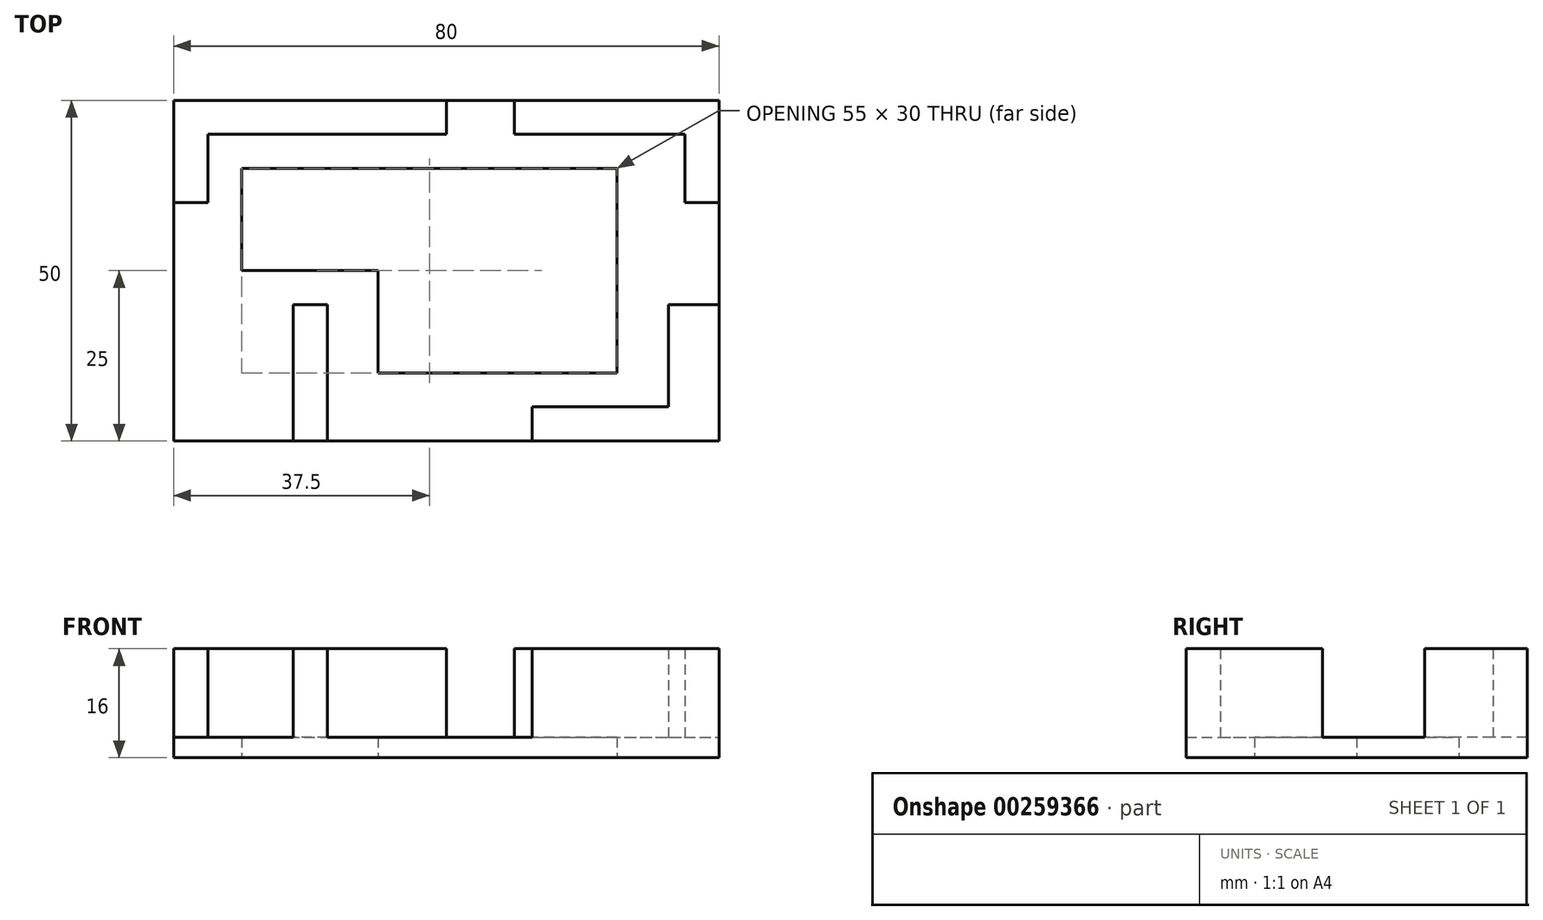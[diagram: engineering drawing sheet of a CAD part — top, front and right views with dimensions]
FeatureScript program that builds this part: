
annotation { "Feature Type Name" : "Feature", "Feature Type Description" : "" }
export const myFeature = defineFeature(function(context is Context, id is Id, definition is map)
    precondition{}
    {
        {
            var Q0;
            Q0=qCreatedBy(makeId("Top.planeOp"),FACE);
            var sketch = newSketch(context, id + "F0", { "sketchPlane" : qUnion([Q0])});
            skLineSegment(sketch, "E0.bottom", {"start": v(40, -25) * mm, "end": v(-40, -25) * mm});
            skLineSegment(sketch, "E0.top", {"start": v(40, 25) * mm, "end": v(-40, 25) * mm});
            skLineSegment(sketch, "E0.left", {"start": v(40, -25) * mm, "end": v(40, 25) * mm});
            skLineSegment(sketch, "E0.right", {"start": v(-40, -25) * mm, "end": v(-40, 25) * mm});
            skPoint(sketch, "E0.middle", {"position": v(0, 0) * mm});
            skSolve(sketch);
        }
        {
            var Q0;
            Q0 = qSketchRegion(id + "F0", true);
            extrude(context, id + "F1", {"entities" : qUnion([Q0]), "depth" : 3 * mm});
        }
        {
            var Q0;
            Q0=qCreatedBy(makeId("Top.planeOp"),FACE);
            var sketch = newSketch(context, id + "F2", { "sketchPlane" : qUnion([Q0])});
            skLineSegment(sketch, "E1", {"start": v(0, 20) * mm, "end": v(0, 25) * mm});
            skLineSegment(sketch, "E2", {"start": v(0, 25) * mm, "end": v(-40, 25) * mm});
            skLineSegment(sketch, "E3", {"start": v(-40, 25) * mm, "end": v(-40, 10) * mm});
            skLineSegment(sketch, "E4", {"start": v(-40, 10) * mm, "end": v(-35, 10) * mm});
            skLineSegment(sketch, "E5", {"start": v(-35, 10) * mm, "end": v(-35, 20) * mm});
            skLineSegment(sketch, "E6", {"start": v(10, 25) * mm, "end": v(40, 25) * mm});
            skLineSegment(sketch, "E7", {"start": v(40, 25) * mm, "end": v(40, 10) * mm});
            skLineSegment(sketch, "E8", {"start": v(40, 10) * mm, "end": v(35, 10) * mm});
            skLineSegment(sketch, "E9", {"start": v(35, 10) * mm, "end": v(35, 20) * mm});
            skLineSegment(sketch, "E10", {"start": v(35, 20) * mm, "end": v(10, 20) * mm});
            skLineSegment(sketch, "E11", {"start": v(10, 20) * mm, "end": v(10, 25) * mm});
            skLineSegment(sketch, "E12", {"start": v(40, -5) * mm, "end": v(40, -25) * mm});
            skLineSegment(sketch, "E13", {"start": v(40, -25) * mm, "end": v(40, -5) * mm});
            skLineSegment(sketch, "E14", {"start": v(40, -5) * mm, "end": v(32.55, -5) * mm});
            skLineSegment(sketch, "E15", {"start": v(32.55, -5) * mm, "end": v(32.55, -20) * mm});
            skLineSegment(sketch, "E16", {"start": v(32.55, -20) * mm, "end": v(12.55, -20) * mm});
            skLineSegment(sketch, "E17", {"start": v(12.55, -20) * mm, "end": v(12.55, -25) * mm});
            skLineSegment(sketch, "E18", {"start": v(12.55, -25) * mm, "end": v(40, -25) * mm});
            skLineSegment(sketch, "E19", {"start": v(-17.45, -25) * mm, "end": v(-22.45, -25) * mm});
            skLineSegment(sketch, "E20", {"start": v(-22.45, -25) * mm, "end": v(-22.45, -20) * mm});
            skLineSegment(sketch, "E21", {"start": v(-22.45, -20) * mm, "end": v(-22.45, -5) * mm});
            skLineSegment(sketch, "E22", {"start": v(-22.45, -5) * mm, "end": v(-17.45, -5) * mm});
            skLineSegment(sketch, "E23", {"start": v(-17.45, -5) * mm, "end": v(-17.45, -25) * mm});
            skLineSegment(sketch, "E24", {"start": v(-35, 20) * mm, "end": v(0, 20) * mm});
            skSolve(sketch);
        }
        {
            var Q0;
            Q0 = qSketchRegion(id + "F2", true);
            extrude(context, id + "F3", {"entities" : qUnion([Q0]), "operationType" : NewBodyOperationType.ADD, "depth" : 16 * mm});
        }
        {
            var Q0;
            Q0=qCreatedBy(makeId("Top.planeOp"),FACE);
            var sketch = newSketch(context, id + "F4", { "sketchPlane" : qUnion([Q0])});
            skLineSegment(sketch, "E25", {"start": v(-10, 0) * mm, "end": v(-30, 0) * mm});
            skLineSegment(sketch, "E26", {"start": v(-30, 0) * mm, "end": v(-30, 15) * mm});
            skLineSegment(sketch, "E27", {"start": v(-30, 15) * mm, "end": v(25, 15) * mm});
            skLineSegment(sketch, "E28", {"start": v(25, 15) * mm, "end": v(25, -15) * mm});
            skLineSegment(sketch, "E29", {"start": v(25, -15) * mm, "end": v(-10, -15) * mm});
            skLineSegment(sketch, "E30", {"start": v(-10, -15) * mm, "end": v(-10, 0) * mm});
            skSolve(sketch);
        }
        {
            var Q0;
            Q0 = qSketchRegion(id + "F4", true);
            extrude(context, id + "F5", {"entities" : qUnion([Q0]), "depth" : 25 * mm});
        }
        {
            var Q0;
            Q0=makeQuery(id+"F5.opExtrude","SWEPT_BODY",BODY,{"disambiguationData":[OSD([sQuery(id+"F4.wireOp",EDGE,"E25"),sQuery(id+"F4.wireOp",EDGE,"E26"),sQuery(id+"F4.wireOp",EDGE,"E27"),sQuery(id+"F4.wireOp",EDGE,"E28"),sQuery(id+"F4.wireOp",EDGE,"E29"),sQuery(id+"F4.wireOp",EDGE,"E30")])]});
            var Q1;
            Q1=makeQuery(id+"F1.opExtrude","SWEPT_BODY",BODY,{"disambiguationData":[OSD([sQuery(id+"F0.wireOp",EDGE,"E0.bottom"),sQuery(id+"F0.wireOp",EDGE,"E0.top"),sQuery(id+"F0.wireOp",EDGE,"E0.left"),sQuery(id+"F0.wireOp",EDGE,"E0.right")])]});
            booleanBodies(context, id + "F6", {"operationType" : BooleanOperationType.SUBTRACTION, "tools" : qUnion([Q0]), "targets" : qUnion([Q1])});
        }
    });
